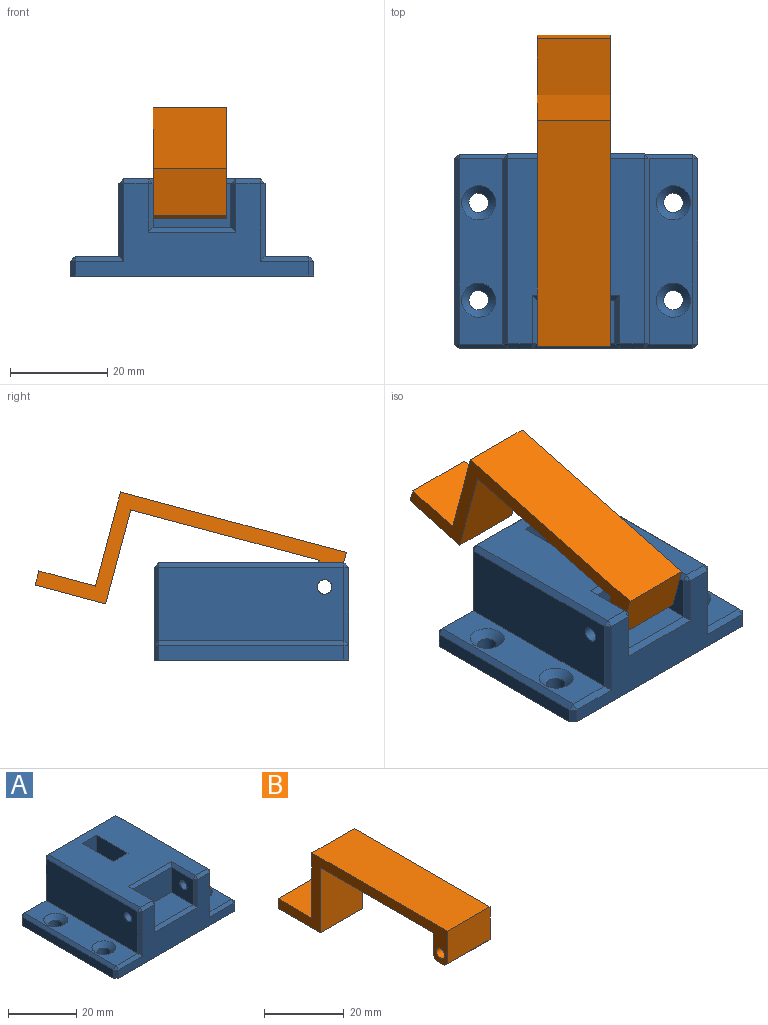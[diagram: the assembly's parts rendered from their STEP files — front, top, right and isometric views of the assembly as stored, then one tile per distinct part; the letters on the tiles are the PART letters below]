
ASSEMBLY  parts=2 mates=1
PART A: 68 faces, bbox 50x40x20 mm
  f0: plane 48x19mm, normal (0,-1,0), area 412mm2, adj f15,f33,f36,f39,f42,f44,f45,f47
  f1: plane 38x28mm, normal (0,0,1), area 806mm2, adj f2,f4,f5,f13,f34,f41,f45,f46
  f2: plane 20x6mm, normal (0,-1,0), area 79.5mm2, adj f1,f5,f13,f15,f18,f19,f20,f21
  f3: plane 38x9mm, normal (0,0,1), area 265mm2, adj f17,f26,f27,f60,f64,f65
  f4: plane 20x6mm, normal (0,1,0), area 79.5mm2, adj f1,f5,f13,f15,f18,f19,f20,f21
  f5: plane 13x6.5mm, normal (1,0,0), area 84.5mm2, adj f1,f2,f4,f19
  f6: plane 38x3mm, normal (1,0,0), area 114mm2, adj f15,f33,f37,f38
  f7: plane 48x19mm, normal (0,1,0), area 592mm2, adj f15,f37,f48,f51,f56,f62,f64,f67
  f8: cylinder r=2mm len=4mm, axis (0,0,-1), area 31.4mm2, adj f15,f29
  f9: cylinder r=2mm len=4mm, axis (0,0,-1), area 31.4mm2, adj f15,f28
  f10: cylinder r=2mm len=4mm, axis (0,0,-1), area 31.4mm2, adj f15,f26
  f11: cylinder r=2mm len=4mm, axis (0,0,-1), area 31.4mm2, adj f15,f27
  f12: plane 38x3mm, normal (-1,0,0), area 114mm2, adj f15,f61,f65,f67
  f13: plane 13x6.5mm, normal (-1,0,0), area 84.5mm2, adj f1,f2,f4,f21
  f14: plane 38x9mm, normal (0,0,1), area 265mm2, adj f16,f28,f29,f38,f39,f48
  f15: plane 50x40mm, normal (0,0,-1), area 1908.7mm2, adj f0,f2,f4,f6,f7,f8,f9,f10
  f16: plane 38x15mm, normal (1,0,0), area 543.3mm2, adj f14,f30,f32,f44,f51,f52
  f17: plane 38x15mm, normal (-1,0,0), area 562.9mm2, adj f3,f31,f57,f58,f62
  f18: plane 13.5x13mm, normal (1,0,0), area 175.5mm2, adj f2,f4,f15,f19
  f19: plane 13x1.5mm, normal (0,0,1), area 19.5mm2, adj f2,f4,f5,f18
  f20: plane 13.5x13mm, normal (-1,0,0), area 155.9mm2, adj f2,f4,f15,f21,f32
  f21: plane 13x1.5mm, normal (0,0,1), area 19.5mm2, adj f2,f4,f13,f20
  f22: plane 9x9mm, normal (1,0,0), area 73.9mm2, adj f24,f25,f31,f46,f47
  f23: plane 9x9mm, normal (-1,0,0), area 73.9mm2, adj f24,f25,f30,f34,f36
  f24: plane 16x9mm, normal (0,-1,0), area 144mm2, adj f22,f23,f25,f41
  f25: plane 16x9mm, normal (0,0,1), area 144mm2, adj f22,f23,f24,f42
  f26: cone r=2mm half-angle=45deg, axis (0,0,1), area 36.7mm2, adj f3,f10
  f27: cone r=2mm half-angle=45deg, axis (0,0,1), area 36.7mm2, adj f3,f11
  f28: cone r=2mm half-angle=45deg, axis (0,0,1), area 36.7mm2, adj f9,f14
  f29: cone r=2mm half-angle=45deg, axis (0,0,1), area 36.7mm2, adj f8,f14
  f30: cylinder r=1.5mm len=7mm, axis (1,0,0), area 66mm2, adj f16,f23
  f31: cylinder r=1.5mm len=7mm, axis (1,0,0), area 66mm2, adj f17,f22
  f32: cylinder r=2.5mm len=13.5mm, axis (1,0,0), area 212.1mm2, adj f16,f20
  f33: plane 3x1mm, normal (0.71,-0.71,0), area 4.2mm2, adj f0,f6,f15,f35
  f34: plane 10x1mm, normal (-0.71,0,0.71), area 13.4mm2, adj f1,f23,f40,f41
  f35: plane 1x1mm, normal (0.58,-0.58,0.58), area 0.9mm2, adj f33,f38,f39
  f36: plane 10x1mm, normal (-0.71,-0.71,0), area 13.4mm2, adj f0,f23,f40,f42
  f37: plane 3x1mm, normal (0.71,0.71,0), area 4.2mm2, adj f6,f7,f15,f43
  f38: plane 38x1mm, normal (0.71,0,0.71), area 53.7mm2, adj f6,f14,f35,f43
  f39: plane 10x1mm, normal (0,-0.71,0.71), area 13.4mm2, adj f0,f14,f35,f44
  f40: plane 1x1mm, normal (-0.58,-0.58,0.58), area 0.9mm2, adj f34,f36,f45
  f41: plane 18x1mm, normal (0,-0.71,0.71), area 24mm2, adj f1,f24,f34,f46
  f42: plane 18x1mm, normal (0,-0.71,0.71), area 24mm2, adj f0,f25,f36,f47
  f43: plane 1x1mm, normal (0.58,0.58,0.58), area 0.9mm2, adj f37,f38,f48
  f44: plane 16x1mm, normal (0.71,-0.71,0), area 21.9mm2, adj f0,f16,f39,f49
  f45: plane 5x1mm, normal (0,-0.71,0.71), area 7.1mm2, adj f0,f1,f40,f49
  f46: plane 10x1mm, normal (0.71,0,0.71), area 13.4mm2, adj f1,f22,f41,f50
  f47: plane 10x1mm, normal (0.71,-0.71,0), area 13.4mm2, adj f0,f22,f42,f50
  f48: plane 10x1mm, normal (0,0.71,0.71), area 13.4mm2, adj f7,f14,f43,f51
  f49: plane 1x1mm, normal (0.58,-0.58,0.58), area 0.9mm2, adj f44,f45,f52
  f50: plane 1x1mm, normal (0.58,-0.58,0.58), area 0.9mm2, adj f46,f47,f53
  f51: plane 16x1mm, normal (0.71,0.71,0), area 21.9mm2, adj f7,f16,f48,f54
  f52: plane 38x1mm, normal (0.71,0,0.71), area 53.7mm2, adj f1,f16,f49,f54
  f53: plane 5x1mm, normal (0,-0.71,0.71), area 7.1mm2, adj f0,f1,f50,f55
  f54: plane 1x1mm, normal (0.58,0.58,0.58), area 0.9mm2, adj f51,f52,f56
  f55: plane 1x1mm, normal (-0.58,-0.58,0.58), area 0.9mm2, adj f53,f57,f58
  f56: plane 28x1mm, normal (0,0.71,0.71), area 39.6mm2, adj f1,f7,f54,f59
  f57: plane 38x1mm, normal (-0.71,0,0.71), area 53.7mm2, adj f1,f17,f55,f59
  f58: plane 16x1mm, normal (-0.71,-0.71,0), area 21.9mm2, adj f0,f17,f55,f60
  f59: plane 1x1mm, normal (-0.58,0.58,0.58), area 0.9mm2, adj f56,f57,f62
  f60: plane 10x1mm, normal (0,-0.71,0.71), area 13.4mm2, adj f0,f3,f58,f63
  f61: plane 3x1mm, normal (-0.71,-0.71,0), area 4.2mm2, adj f0,f12,f15,f63
  f62: plane 16x1mm, normal (-0.71,0.71,0), area 21.9mm2, adj f7,f17,f59,f64
  f63: plane 1x1mm, normal (-0.58,-0.58,0.58), area 0.9mm2, adj f60,f61,f65
  f64: plane 10x1mm, normal (0,0.71,0.71), area 13.4mm2, adj f3,f7,f62,f66
  f65: plane 38x1mm, normal (-0.71,0,0.71), area 53.7mm2, adj f3,f12,f63,f66
  f66: plane 1x1mm, normal (-0.58,0.58,0.58), area 0.9mm2, adj f64,f65,f67
  f67: plane 3x1mm, normal (-0.71,0.71,0), area 4.2mm2, adj f7,f12,f15,f66
PART B: 15 faces, bbox 15x60x23 mm
  f0: plane 40x15mm, normal (0,0,-1), area 600mm2, adj f1,f9,f11,f12
  f1: plane 20x15mm, normal (0,-1,0), area 300mm2, adj f0,f2,f11,f12
  f2: plane 15x15mm, normal (0,0,-1), area 225mm2, adj f1,f3,f11,f12
  f3: plane 15x3mm, normal (0,1,0), area 45mm2, adj f2,f4,f11,f12
  f4: plane 15x12mm, normal (0,0,1), area 180mm2, adj f3,f5,f11,f12
  f5: plane 20x15mm, normal (0,1,0), area 300mm2, adj f4,f6,f11,f12
  f6: plane 48x15mm, normal (0,0,1), area 720mm2, adj f5,f7,f11,f12
  f7: plane 15x10mm, normal (0,-1,0), area 150mm2, adj f6,f11,f12,f13
  f8: plane 15x3mm, normal (0,0,-1), area 45mm2, adj f11,f12,f13,f14
  f9: plane 15x7mm, normal (0,1,0), area 105mm2, adj f0,f11,f12,f14
  f10: cylinder r=1.5mm len=15mm, axis (-1,0,0), area 141.4mm2, adj f11,f12
  f11: plane 60x23mm, normal (1,0,0), area 271.9mm2, adj f0,f1,f2,f3,f4,f5,f6,f7
  f12: plane 60x23mm, normal (-1,0,0), area 271.9mm2, adj f0,f1,f2,f3,f4,f5,f6,f7
  f13: plane 15x1mm, normal (0,-0.71,-0.71), area 21.2mm2, adj f7,f8,f11,f12
  f14: plane 15x1mm, normal (0,0.71,-0.71), area 21.2mm2, adj f8,f9,f11,f12
PLACE A t=(13,-30.59,-20.4)mm
PLACE B rot(axis=(1,0,0),15deg) t=(-25,-27.22,-16.01)mm
MATE revolute B.f10 <-> A.f30  axis (-1,0,0) through (5,-45.59,-5.4)mm
